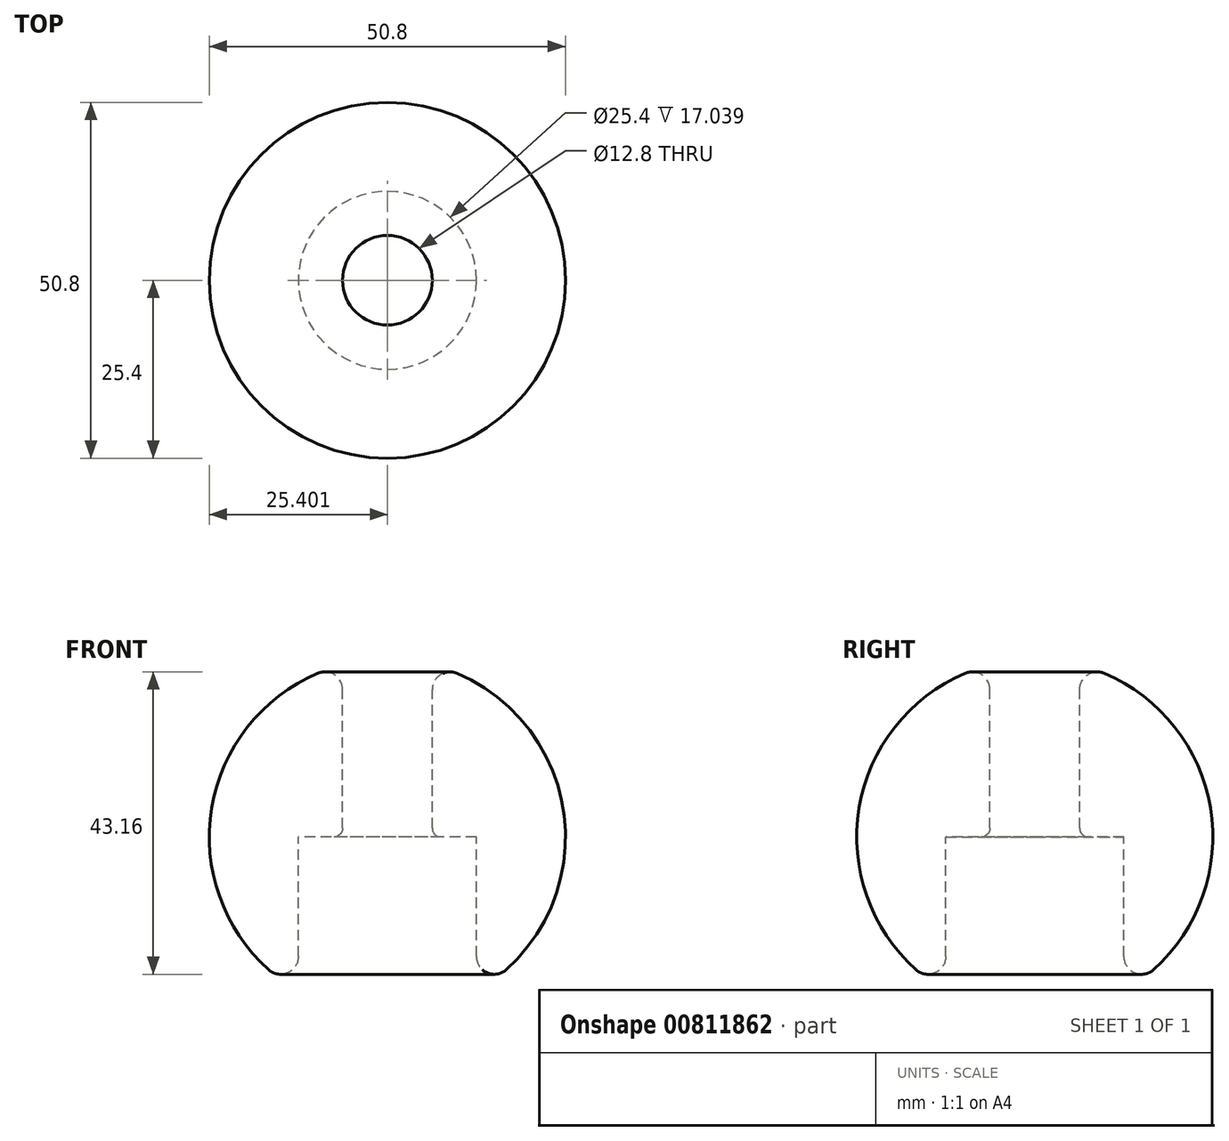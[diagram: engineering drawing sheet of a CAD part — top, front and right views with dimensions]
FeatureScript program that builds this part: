
annotation { "Feature Type Name" : "Feature", "Feature Type Description" : "" }
export const myFeature = defineFeature(function(context is Context, id is Id, definition is map)
    precondition{}
    {
        {
            var Q0;
            Q0=qCreatedBy(makeId("Front.planeOp"),FACE);
            var sketch = newSketch(context, id + "F0", { "sketchPlane" : qUnion([Q0])});
            skPoint(sketch, "E0.orphan", {"position": v(0.04, 0) * mm});
            skPoint(sketch, "E1.MirrorCS.start.orphan", {"position": v(0, 0) * mm});
            skLineSegment(sketch, "E2", {"start": v(0.04, 25.4) * mm, "end": v(0.04, 0) * mm});
            skArc(sketch, "E3", {"start": v(-9.89, 23.38) * mm, "mid": v(-25.02, 4.15) * mm, "end": v(-16.9, -18.93) * mm});
            skLineSegment(sketch, "E4", {"start": v(-6.36, 21.04) * mm, "end": v(-6.36, 1.27) * mm});
            skLineSegment(sketch, "E5", {"start": v(-12.66, 0) * mm, "end": v(-12.66, -17.04) * mm});
            skLineSegment(sketch, "E6", {"start": v(-12.66, 0) * mm, "end": v(-7.63, 0) * mm});
            skPoint(sketch, "E7.orphan", {"position": v(-12.66, -29.6) * mm});
            skPoint(sketch, "E8.trimOffspring.end.orphan", {"position": v(-6.3, -29.37) * mm});
            skArc(sketch, "E9.filletArc", {"start": v(-6.36, 21.04) * mm, "mid": v(-7.5, 23.16) * mm, "end": v(-9.89, 23.38) * mm});
            skArc(sketch, "E10.filletArc", {"start": v(-16.9, -18.93) * mm, "mid": v(-14.16, -19.36) * mm, "end": v(-12.66, -17.04) * mm});
            skPoint(sketch, "E11.visualSharp", {"position": v(-6.36, 0) * mm});
            skArc(sketch, "E11.filletArc", {"start": v(-7.63, 0) * mm, "mid": v(-6.73, 0.37) * mm, "end": v(-6.36, 1.27) * mm});
            skSolve(sketch);
        }
        {
            var Q0;
            Q0=qCreatedBy(makeId("Front.planeOp"),FACE);
            var sketch = newSketch(context, id + "F1", { "sketchPlane" : qUnion([Q0])});
            skLineSegment(sketch, "E12", {"start": v(0.04, 25.4) * mm, "end": v(0.04, -25.4) * mm});
            skSolve(sketch);
        }
        {
            var Q0;
            Q0 = qSketchRegion(id + "F0", true);
            var Q1;
            Q1=sQuery(id+"F1.wireOp",EDGE,"E12");
            revolve(context, id + "F2", {"surfaceOperationType" : NewSurfaceOperationType.NEW, "entities" : qUnion([Q0]), "axis" : qUnion([Q1]), "revolveType" : RevolveType.FULL});
        }
    });
